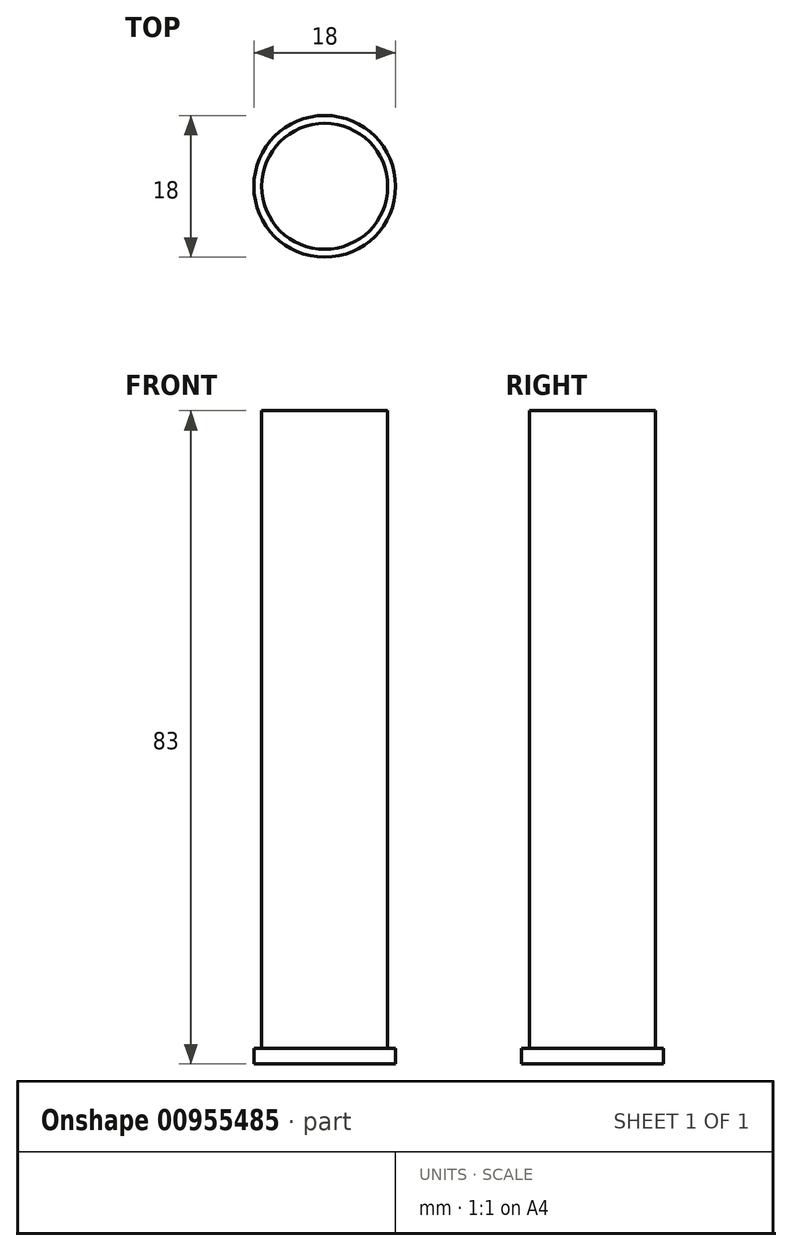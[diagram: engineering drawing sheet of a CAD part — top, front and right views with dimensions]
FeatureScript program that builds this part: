
annotation { "Feature Type Name" : "Feature", "Feature Type Description" : "" }
export const myFeature = defineFeature(function(context is Context, id is Id, definition is map)
    precondition{}
    {
        {
            var Q0;
            Q0=qCreatedBy(makeId("Front.planeOp"),FACE);
            var sketch = newSketch(context, id + "F0", { "sketchPlane" : qUnion([Q0])});
            skLineSegment(sketch, "E0", {"start": v(0, 0) * mm, "end": v(9, 0) * mm});
            skLineSegment(sketch, "E1", {"start": v(9, 0) * mm, "end": v(9, 2) * mm});
            skLineSegment(sketch, "E2", {"start": v(9, 2) * mm, "end": v(8, 2) * mm});
            skLineSegment(sketch, "E3", {"start": v(8, 2) * mm, "end": v(8, 83) * mm});
            skLineSegment(sketch, "E4", {"start": v(8, 83) * mm, "end": v(0, 83) * mm});
            skLineSegment(sketch, "E5", {"start": v(0, 83) * mm, "end": v(0, 0) * mm});
            skSolve(sketch);
        }
        {
            var Q0;
            Q0=makeQuery(id+"F0.imprint","IMPRINT",FACE,{"disambiguationData":[TD([[makeQuery(id+"F0.imprint","IMPRINT",EDGE,{"derivedFrom":sQuery(id+"F0.wireOp",EDGE,"E0")}),1.0]])]});
            var Q1;
            Q1=sQuery(id+"F0.wireOp",EDGE,"E5");
            revolve(context, id + "F1", {"surfaceOperationType" : NewSurfaceOperationType.NEW, "entities" : qUnion([Q0]), "axis" : qUnion([Q1]), "revolveType" : RevolveType.FULL});
        }
    });
